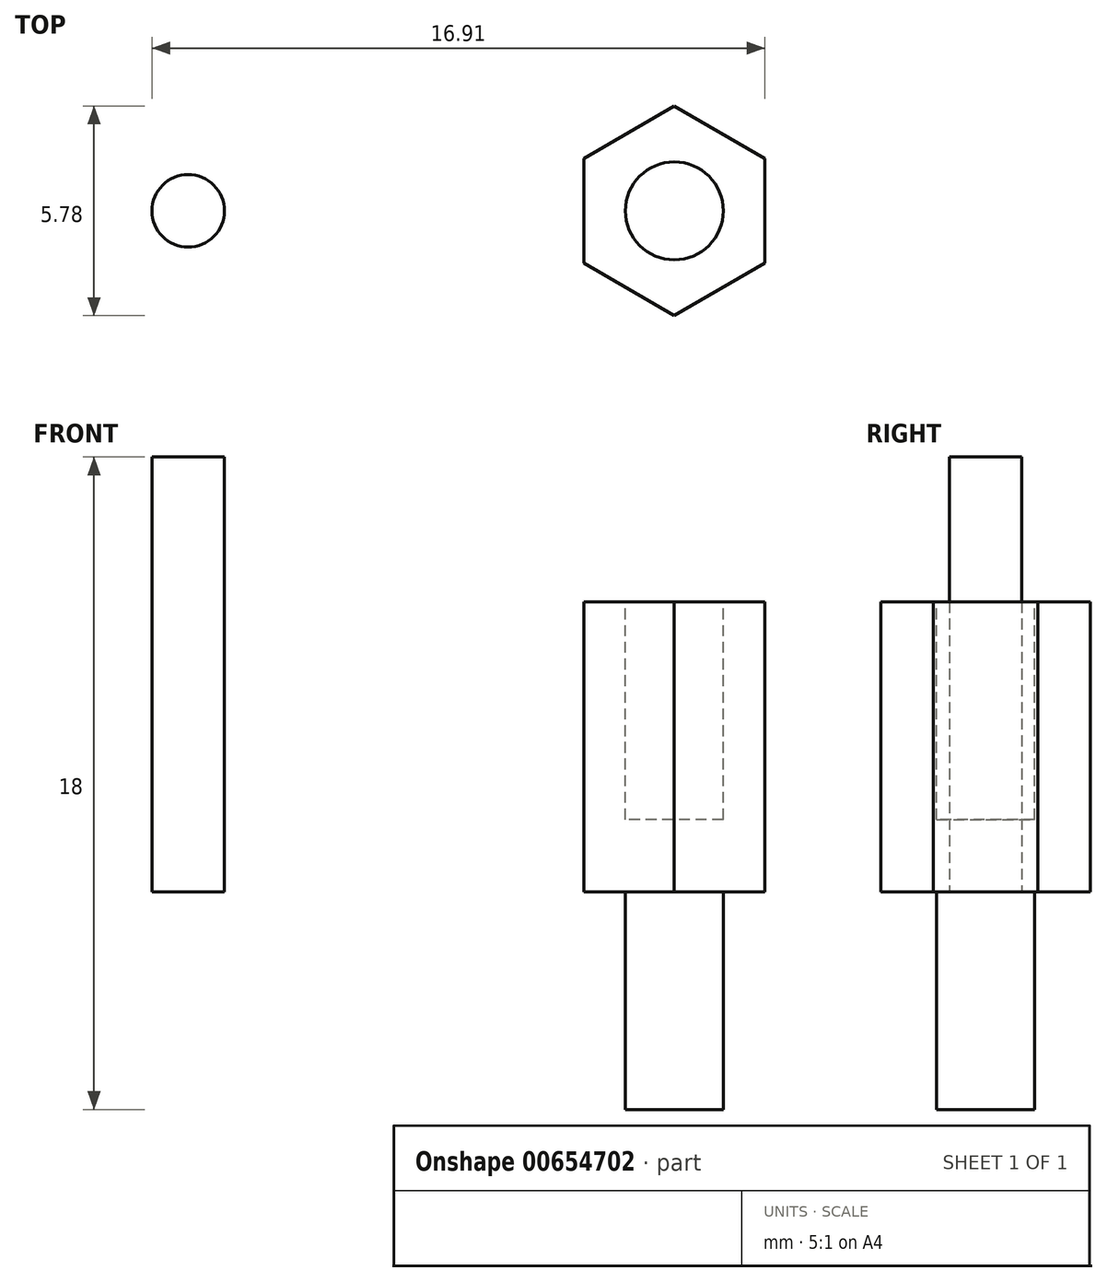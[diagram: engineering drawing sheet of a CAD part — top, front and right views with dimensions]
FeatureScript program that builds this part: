
annotation { "Feature Type Name" : "Feature", "Feature Type Description" : "" }
export const myFeature = defineFeature(function(context is Context, id is Id, definition is map)
    precondition{}
    {
        {
            var Q0;
            Q0=qCreatedBy(makeId("Top.planeOp"),FACE);
            var sketch = newSketch(context, id + "F0", { "sketchPlane" : qUnion([Q0])});
            skCircle(sketch, "E0", {"center": v(0, 0) * mm, "radius": 1 * mm});
            skSolve(sketch);
        }
        {
            var Q0;
            Q0=makeQuery(id+"F0.imprint","IMPRINT",FACE,{"disambiguationData":[TD([[makeQuery(id+"F0.imprint","IMPRINT",EDGE,{"derivedFrom":sQuery(id+"F0.wireOp",EDGE,"E0")}),1.0]])]});
            extrude(context, id + "F1", {"entities" : qUnion([Q0]), "depth" : 12 * mm, "offsetDistance" : 25 * mm});
        }
        {
            var Q0;
            Q0=qCreatedBy(makeId("Top.planeOp"),FACE);
            var sketch = newSketch(context, id + "F2", { "sketchPlane" : qUnion([Q0])});
            skCircle(sketch, "E1.cCircle", {"center": v(13.41, 0) * mm, "radius": 2.5 * mm, "construction": true});
            skLineSegment(sketch, "E1.0", {"start": v(15.91, 1.44) * mm, "end": v(15.91, -1.44) * mm});
            skLineSegment(sketch, "E1.1", {"start": v(15.91, -1.44) * mm, "end": v(13.41, -2.89) * mm});
            skLineSegment(sketch, "E1.2", {"start": v(13.41, -2.89) * mm, "end": v(10.91, -1.44) * mm});
            skLineSegment(sketch, "E1.3", {"start": v(10.91, -1.44) * mm, "end": v(10.91, 1.44) * mm});
            skLineSegment(sketch, "E1.4", {"start": v(10.91, 1.44) * mm, "end": v(13.41, 2.89) * mm});
            skLineSegment(sketch, "E1.5", {"start": v(13.41, 2.89) * mm, "end": v(15.91, 1.44) * mm});
            skPoint(sketch, "E1.0.midPoint", {"position": v(15.91, 0) * mm});
            skSolve(sketch);
        }
        {
            var Q0;
            Q0 = qSketchRegion(id + "F2", true);
            extrude(context, id + "F3", {"entities" : qUnion([Q0]), "depth" : 8 * mm, "offsetDistance" : 25 * mm});
        }
        {
            var Q0;
            Q0=makeQuery(id+"F3.opExtrude","CAP_FACE",FACE,{"disambiguationData":[OSD([sQuery(id+"F2.wireOp",EDGE,"E1.0"),sQuery(id+"F2.wireOp",EDGE,"E1.1"),sQuery(id+"F2.wireOp",EDGE,"E1.2"),sQuery(id+"F2.wireOp",EDGE,"E1.3"),sQuery(id+"F2.wireOp",EDGE,"E1.4"),sQuery(id+"F2.wireOp",EDGE,"E1.5")])],"isStart":false});
            var sketch = newSketch(context, id + "F4", { "sketchPlane" : qUnion([Q0])});
            skCircle(sketch, "E2", {"center": v(13.41, 0) * mm, "radius": 1.35 * mm});
            skLineSegment(sketch, "E3", {"start": v(13.41, 2.89) * mm, "end": v(13.41, -2.89) * mm, "construction": true});
            skLineSegment(sketch, "E4", {"start": v(10.91, 1.44) * mm, "end": v(15.91, -1.44) * mm, "construction": true});
            skSolve(sketch);
        }
        {
            var Q0;
            Q0=makeQuery(id+"F4.imprint","IMPRINT",FACE,{"disambiguationData":[TD([[makeQuery(id+"F4.imprint","IMPRINT",EDGE,{"derivedFrom":sQuery(id+"F4.wireOp",EDGE,"E2")}),1.0]])]});
            extrude(context, id + "F5", {"entities" : qUnion([Q0]), "operationType" : NewBodyOperationType.REMOVE, "oppositeDirection" : true, "depth" : 6 * mm, "offsetDistance" : 25 * mm});
        }
        {
            var Q0;
            Q0=makeQuery(id+"F3.opExtrude","CAP_FACE",FACE,{"disambiguationData":[OSD([sQuery(id+"F2.wireOp",EDGE,"E1.0"),sQuery(id+"F2.wireOp",EDGE,"E1.1"),sQuery(id+"F2.wireOp",EDGE,"E1.2"),sQuery(id+"F2.wireOp",EDGE,"E1.3"),sQuery(id+"F2.wireOp",EDGE,"E1.4"),sQuery(id+"F2.wireOp",EDGE,"E1.5")])],"isStart":true});
            var sketch = newSketch(context, id + "F6", { "sketchPlane" : qUnion([Q0])});
            skLineSegment(sketch, "E5", {"start": v(13.41, 2.89) * mm, "end": v(13.41, -2.89) * mm, "construction": true});
            skLineSegment(sketch, "E6", {"start": v(10.91, -1.44) * mm, "end": v(15.91, 1.44) * mm, "construction": true});
            skCircle(sketch, "E7", {"center": v(13.41, 0) * mm, "radius": 1.35 * mm});
            skSolve(sketch);
        }
        {
            var Q0;
            Q0 = qSketchRegion(id + "F6", true);
            extrude(context, id + "F7", {"entities" : qUnion([Q0]), "operationType" : NewBodyOperationType.ADD, "depth" : 6 * mm, "offsetDistance" : 25 * mm});
        }
    });
